# Revit family: Domotics-DomesticRanges-GEWISS-SYSTEM_DATA-TV_SAT_SOCKET
name_source: partatom
category: Apparecchi elettrici
revit_build: Autodesk Revit 2016 (Build: 20161004_0715(x64)
units: mm (PartAtom-declared; Revit-internal decimal feet)

## family parameters
Condiviso = Sì
Host = Superficie
Mantenere orientamento annotazione = Sì
Punto di calcolo locali = Sì
Quota connettore circolare = Usa diametro
Taglio con vuoti quando caricato = Sì
Tipo di parte = Normale

## types (8) — shared parameters
Carico apparente = 0 VA
Catalogue = DOMOTICS
Catalogue Range = SYSTEM - DOMESTIC RANGE
Description. = TV/SAT socket-outlet
Electrocod = 0131
For connector type = F-Female
Frequency = 5-2400 MHz
IDF = 1b25a30f-1712-4c6f-8359-4124d0180e15
IDT = a744499d-be5a-4e59-b39c-2c1bf6a8619f
Immagine tipo = GW21391.jpg
N. poli = 1
No. SYSTEM modules = 1
Produttore = GEWISS S.p.A.
Prospetto di default = 1219 mm
SEO = Socket outlet
Shielding = Class A
Technical sheet = https://www.gewiss.com
Tipo_ = SYSTEM PRESE TV-SAT_GENERICO : GW21396 Presa TV/SAT passante attenuata 5 dB conn. F-femmina nero
URL = https://www.gewiss.com
Version file RFA = 19.4
Volt = 230 V

## per-type parameters (varying)
| type | Attenuation | Colour | Description: | Descrizione | EAN code | Modello | Type |
| GW20392 - THR.TV/SAT SOCK.10DB F-FEMALE SY/WT | 10 dB | White | Feedtrough | THR.TV/SAT SOCK.10DB F-FEMALE SY/WT | 8011564078949 | GW20392 |  |
| GW21393 - THR.TV/SAT SOCK.14DB F-FEMALE SY/BK | 14 dB | Black | Feedtrough | THR.TV/SAT SOCK.14DB F-FEMALE SY/BK | 8011564128644 | GW21393 |  |
| GW20393 - THR.TV/SAT SOCK.14DB F-FEMALE SY/WT | 14 dB | White | Feedtrough | THR.TV/SAT SOCK.14DB F-FEMALE SY/WT | 8011564078956 | GW20393 |  |
| GW20391 - DIRECT TV/SAT SOCKET F-FEMALE C.SY/WT | 0 dB | White | Direct | DIRECT TV/SAT SOCKET F-FEMALE C.SY/WT | 8011564078932 | GW20391 | With passage of current |
| GW21392 - THR.TV/SAT SOCK.10DB F-FEMALE SY/BK | 10 dB | Black | Feedtrough | THR.TV/SAT SOCK.10DB F-FEMALE SY/BK | 8011564128637 | GW21392 |  |
| GW21396 - THR.TV/SAT SOCK.5 DB F-FEMALE SY/BK | 5 dB | Black | Feedtrough | THR.TV/SAT SOCK.5 DB F-FEMALE SY/BK | 8011564128620 | GW21396 |  |
| GW21391 - DIRECT TV/SAT SOCKET F-FEMALE C.SY/BK | 0 dB | Black | Direct | DIRECT TV/SAT SOCKET F-FEMALE C.SY/BK | 8011564128613 | GW21391 | With passage of current |
| GW20396 - THR.TV/SAT SOCK.5 DB F-FEMALE SY/WT | 5 dB | White | Feedtrough | THR.TV/SAT SOCK.5 DB F-FEMALE SY/WT | 8011564078987 | GW20396 |  |

## geometry (parser evidence)
native form markers: Sweep x1
no freeform markers — native parametric forms only
